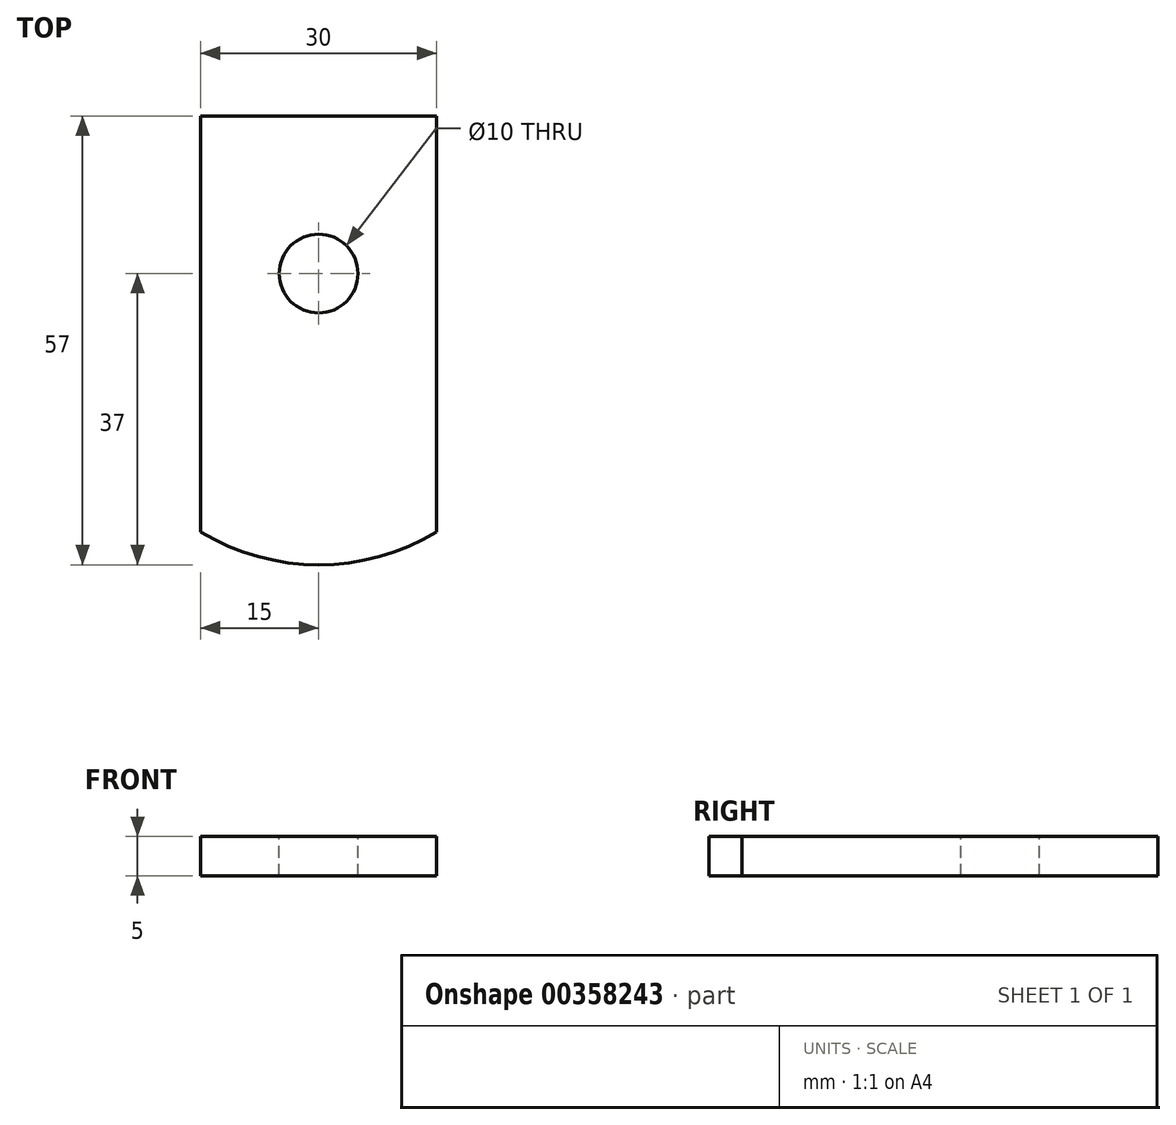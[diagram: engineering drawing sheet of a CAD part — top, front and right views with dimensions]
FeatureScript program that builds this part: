
annotation { "Feature Type Name" : "Feature", "Feature Type Description" : "" }
export const myFeature = defineFeature(function(context is Context, id is Id, definition is map)
    precondition{}
    {
        {
            var Q0;
            Q0=qCreatedBy(makeId("Top.planeOp"),FACE);
            var sketch = newSketch(context, id + "F0", { "sketchPlane" : qUnion([Q0])});
            skLineSegment(sketch, "E0.top", {"start": v(15, 28.5) * mm, "end": v(-15, 28.5) * mm});
            skLineSegment(sketch, "E0.left", {"start": v(15, -24.32) * mm, "end": v(15, 28.5) * mm});
            skLineSegment(sketch, "E0.right", {"start": v(-15, -24.32) * mm, "end": v(-15, 28.5) * mm});
            skPoint(sketch, "E0.middle", {"position": v(0, 0) * mm});
            skArc(sketch, "E1", {"start": v(-15, -24.32) * mm, "mid": v(0, -28.5) * mm, "end": v(15, -24.32) * mm});
            skPoint(sketch, "E2.orphan", {"position": v(15, -28.5) * mm});
            skPoint(sketch, "E3.orphan", {"position": v(-15, -28.5) * mm});
            skSolve(sketch);
        }
        {
            var Q0;
            Q0 = qSketchRegion(id + "F0", true);
            extrude(context, id + "F1", {"entities" : qUnion([Q0]), "depth" : 5 * mm});
        }
        {
            var Q0;
            Q0=makeQuery(id+"F1.opExtrude","CAP_FACE",FACE,{"disambiguationData":[OSD([sQuery(id+"F0.wireOp",EDGE,"E0.bottom"),sQuery(id+"F0.wireOp",EDGE,"E0.top"),sQuery(id+"F0.wireOp",EDGE,"E0.left"),sQuery(id+"F0.wireOp",EDGE,"E0.right")])],"isStart":false});
            var sketch = newSketch(context, id + "F2", { "sketchPlane" : qUnion([Q0])});
            skCircle(sketch, "E4", {"center": v(0, 8.5) * mm, "radius": 5 * mm});
            skSolve(sketch);
        }
        {
            var Q0;
            Q0 = qSketchRegion(id + "F2", true);
            extrude(context, id + "F3", {"entities" : qUnion([Q0]), "operationType" : NewBodyOperationType.REMOVE, "oppositeDirection" : true, "depth" : 5 * mm});
        }
    });
